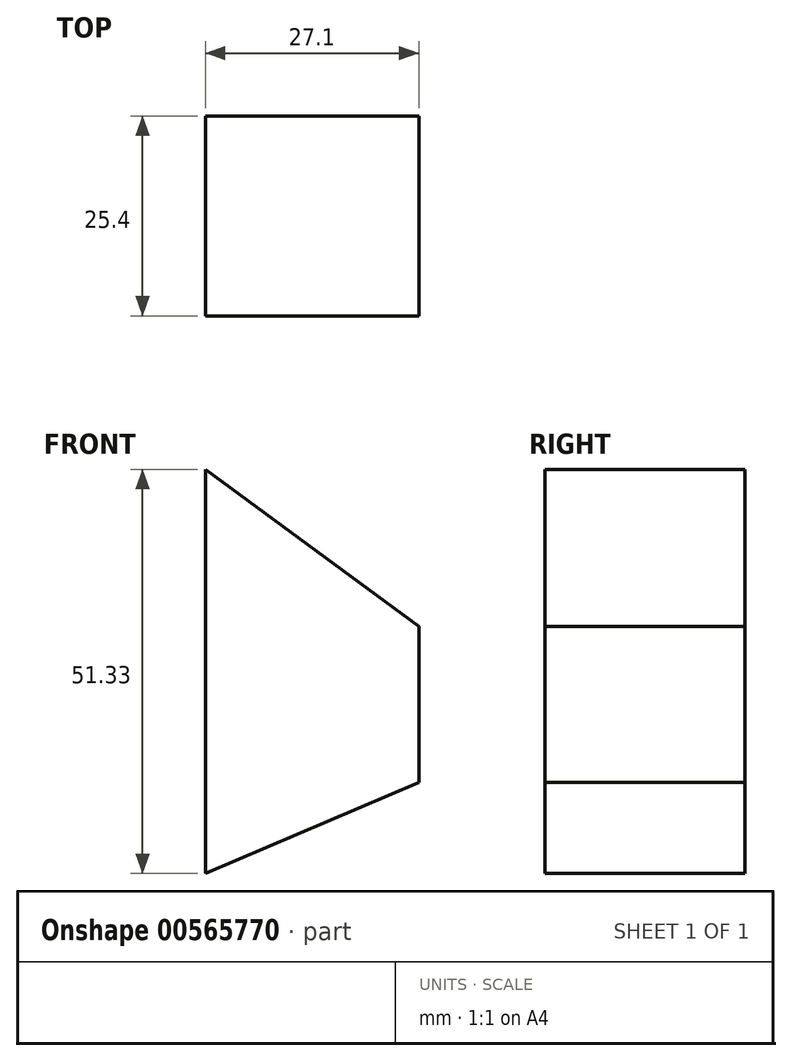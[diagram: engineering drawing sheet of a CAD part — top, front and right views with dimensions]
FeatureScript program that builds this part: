
annotation { "Feature Type Name" : "Feature", "Feature Type Description" : "" }
export const myFeature = defineFeature(function(context is Context, id is Id, definition is map)
    precondition{}
    {
        {
            var Q0;
            Q0=qCreatedBy(makeId("Front.planeOp"),FACE);
            var sketch = newSketch(context, id + "F0", { "sketchPlane" : qUnion([Q0])});
            skLineSegment(sketch, "E0", {"start": v(101.09, 11.6) * mm, "end": v(101.09, 31.4) * mm});
            skLineSegment(sketch, "E1", {"start": v(101.09, 31.4) * mm, "end": v(74, 51.33) * mm});
            skLineSegment(sketch, "E2", {"start": v(74, 51.33) * mm, "end": v(74, 0) * mm});
            skLineSegment(sketch, "E3", {"start": v(74, 0) * mm, "end": v(101.09, 11.6) * mm});
            skSolve(sketch);
        }
        {
            var Q0;
            Q0 = qSketchRegion(id + "F0", true);
            extrude(context, id + "F1", {"entities" : qUnion([Q0]), "oppositeDirection" : true, "depth" : 25.4 * mm, "offsetDistance" : 25.4 * mm});
        }
    });
